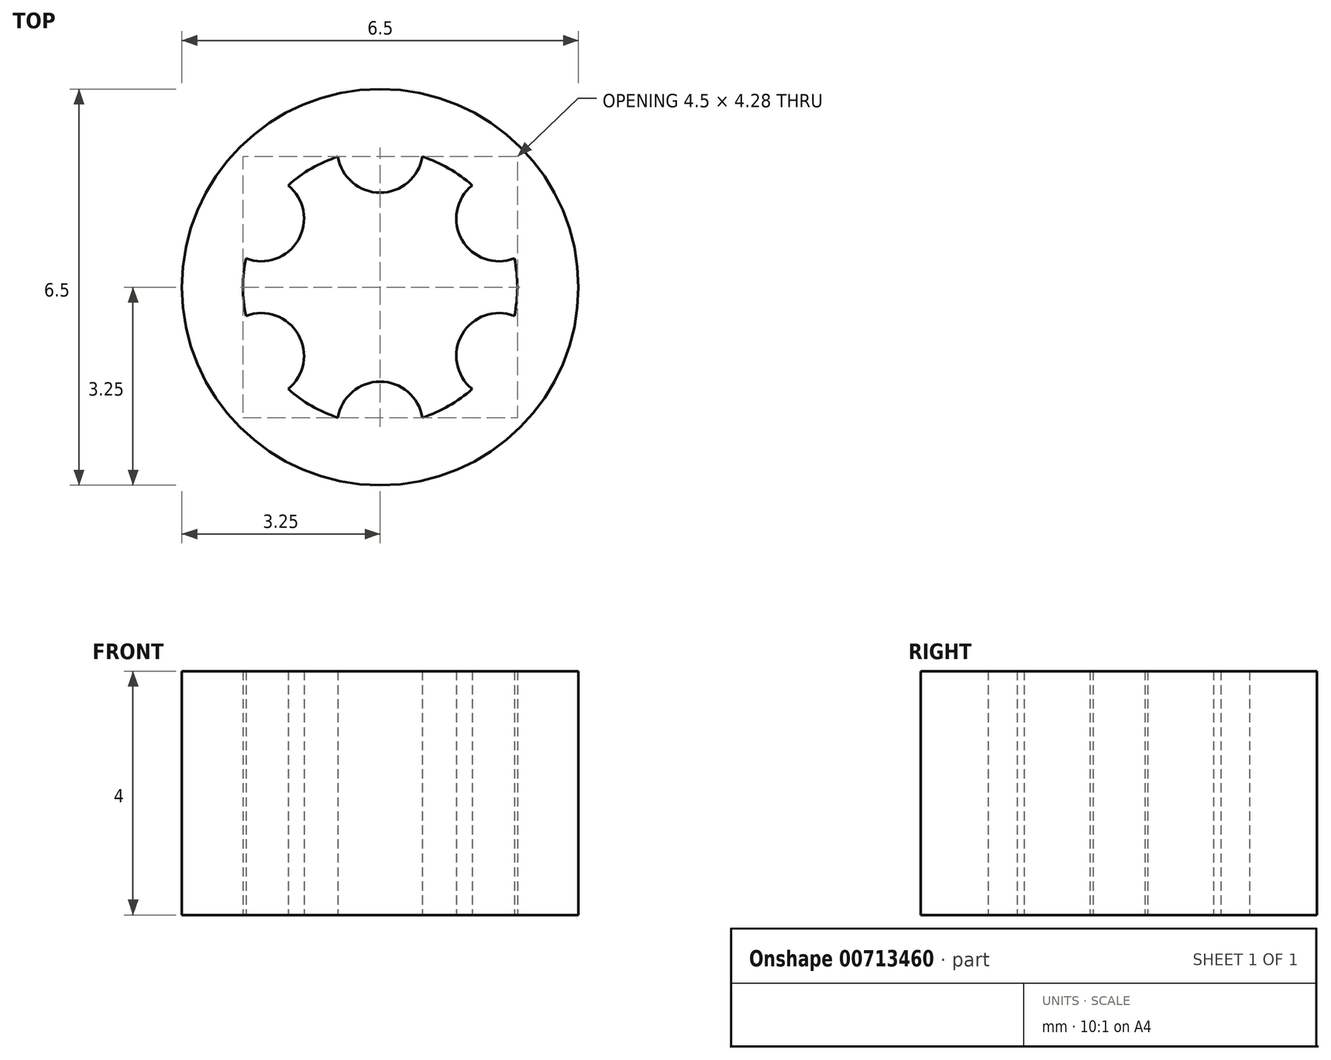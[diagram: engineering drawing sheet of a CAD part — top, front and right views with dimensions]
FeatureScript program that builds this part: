
annotation { "Feature Type Name" : "Feature", "Feature Type Description" : "" }
export const myFeature = defineFeature(function(context is Context, id is Id, definition is map)
    precondition{}
    {
        {
            var Q0;
            Q0=qCreatedBy(makeId("Top.planeOp"),FACE);
            var sketch = newSketch(context, id + "F0", { "sketchPlane" : qUnion([Q0])});
            skCircle(sketch, "E0", {"center": v(0, 0) * mm, "radius": 2.25 * mm});
            skCircle(sketch, "E1", {"center": v(0, 0) * mm, "radius": 3.25 * mm});
            skCircle(sketch, "E2", {"center": v(0, 2.25) * mm, "radius": 0.7 * mm});
            skCircle(sketch, "E3.1.0", {"center": v(-1.95, 1.13) * mm, "radius": 0.7 * mm});
            skCircle(sketch, "E3.2.0", {"center": v(-1.95, -1.12) * mm, "radius": 0.7 * mm});
            skCircle(sketch, "E3.3.0", {"center": v(0, -2.25) * mm, "radius": 0.7 * mm});
            skCircle(sketch, "E3.4.0", {"center": v(1.95, -1.13) * mm, "radius": 0.7 * mm});
            skCircle(sketch, "E3.5.0", {"center": v(1.95, 1.13) * mm, "radius": 0.7 * mm});
            skSolve(sketch);
        }
        {
            var Q0;
            Q0=qSketchRegion(id+"F0",true);
            var Q1;
            {var subQ0=sQuery(id+"F0.wireOp",EDGE,"E3.1.0");var subQ1=sQuery(id+"F0.wireOp",EDGE,"E0");var subQ2=makeQuery(id+"F0.imprint","INTERSECT",VERTEX,{"disambiguationData":[OD(0.0)],"derivedFrom":[subQ1,subQ0]});Q1=makeQuery(id+"F0.imprint","IMPRINT",FACE,{"disambiguationData":[TD([[makeQuery(id+"F0.imprint","IMPRINT",EDGE,{"disambiguationData":[TD([[subQ2,-1.0]])],"derivedFrom":subQ1}),1.0]])]});}
            var Q2;
            {var subQ0=sQuery(id+"F0.wireOp",EDGE,"E3.1.0");var subQ1=sQuery(id+"F0.wireOp",EDGE,"E0");var subQ2=makeQuery(id+"F0.imprint","INTERSECT",VERTEX,{"disambiguationData":[OD(0.0)],"derivedFrom":[subQ1,subQ0]});Q2=makeQuery(id+"F0.imprint","IMPRINT",FACE,{"disambiguationData":[TD([[makeQuery(id+"F0.imprint","IMPRINT",EDGE,{"disambiguationData":[TD([[subQ2,-1.0]])],"derivedFrom":subQ1}),-1.0]])]});}
            var Q3;
            {var subQ0=sQuery(id+"F0.wireOp",EDGE,"E2");var subQ1=sQuery(id+"F0.wireOp",EDGE,"E0");var subQ2=makeQuery(id+"F0.imprint","INTERSECT",VERTEX,{"disambiguationData":[OD(0.0)],"derivedFrom":[subQ1,subQ0]});Q3=makeQuery(id+"F0.imprint","IMPRINT",FACE,{"disambiguationData":[TD([[makeQuery(id+"F0.imprint","IMPRINT",EDGE,{"disambiguationData":[TD([[subQ2,-1.0]])],"derivedFrom":subQ1}),-1.0]])]});}
            var Q4;
            {var subQ0=sQuery(id+"F0.wireOp",EDGE,"E2");var subQ1=sQuery(id+"F0.wireOp",EDGE,"E0");var subQ2=makeQuery(id+"F0.imprint","INTERSECT",VERTEX,{"disambiguationData":[OD(0.0)],"derivedFrom":[subQ1,subQ0]});Q4=makeQuery(id+"F0.imprint","IMPRINT",FACE,{"disambiguationData":[TD([[makeQuery(id+"F0.imprint","IMPRINT",EDGE,{"disambiguationData":[TD([[subQ2,-1.0]])],"derivedFrom":subQ1}),1.0]])]});}
            var Q5;
            {var subQ0=sQuery(id+"F0.wireOp",EDGE,"E3.5.0");var subQ1=sQuery(id+"F0.wireOp",EDGE,"E0");var subQ2=makeQuery(id+"F0.imprint","INTERSECT",VERTEX,{"disambiguationData":[OD(0.0)],"derivedFrom":[subQ1,subQ0]});Q5=makeQuery(id+"F0.imprint","IMPRINT",FACE,{"disambiguationData":[TD([[makeQuery(id+"F0.imprint","IMPRINT",EDGE,{"disambiguationData":[TD([[subQ2,1.0]])],"derivedFrom":subQ1}),-1.0]])]});}
            var Q6;
            {var subQ0=sQuery(id+"F0.wireOp",EDGE,"E3.5.0");var subQ1=sQuery(id+"F0.wireOp",EDGE,"E0");var subQ2=makeQuery(id+"F0.imprint","INTERSECT",VERTEX,{"disambiguationData":[OD(0.0)],"derivedFrom":[subQ1,subQ0]});Q6=makeQuery(id+"F0.imprint","IMPRINT",FACE,{"disambiguationData":[TD([[makeQuery(id+"F0.imprint","IMPRINT",EDGE,{"disambiguationData":[TD([[subQ2,1.0]])],"derivedFrom":subQ1}),1.0]])]});}
            var Q7;
            {var subQ0=sQuery(id+"F0.wireOp",EDGE,"E3.4.0");var subQ1=sQuery(id+"F0.wireOp",EDGE,"E0");var subQ2=makeQuery(id+"F0.imprint","INTERSECT",VERTEX,{"disambiguationData":[OD(0.0)],"derivedFrom":[subQ1,subQ0]});Q7=makeQuery(id+"F0.imprint","IMPRINT",FACE,{"disambiguationData":[TD([[makeQuery(id+"F0.imprint","IMPRINT",EDGE,{"disambiguationData":[TD([[subQ2,-1.0]])],"derivedFrom":subQ1}),-1.0]])]});}
            var Q8;
            {var subQ0=sQuery(id+"F0.wireOp",EDGE,"E3.3.0");var subQ1=sQuery(id+"F0.wireOp",EDGE,"E0");var subQ2=makeQuery(id+"F0.imprint","INTERSECT",VERTEX,{"disambiguationData":[OD(0.0)],"derivedFrom":[subQ1,subQ0]});Q8=makeQuery(id+"F0.imprint","IMPRINT",FACE,{"disambiguationData":[TD([[makeQuery(id+"F0.imprint","IMPRINT",EDGE,{"disambiguationData":[TD([[subQ2,-1.0]])],"derivedFrom":subQ1}),-1.0]])]});}
            var Q9;
            {var subQ0=sQuery(id+"F0.wireOp",EDGE,"E3.2.0");var subQ1=sQuery(id+"F0.wireOp",EDGE,"E0");var subQ2=makeQuery(id+"F0.imprint","INTERSECT",VERTEX,{"disambiguationData":[OD(0.0)],"derivedFrom":[subQ1,subQ0]});Q9=makeQuery(id+"F0.imprint","IMPRINT",FACE,{"disambiguationData":[TD([[makeQuery(id+"F0.imprint","IMPRINT",EDGE,{"disambiguationData":[TD([[subQ2,-1.0]])],"derivedFrom":subQ1}),-1.0]])]});}
            var Q10;
            {var subQ0=sQuery(id+"F0.wireOp",EDGE,"E3.3.0");var subQ1=sQuery(id+"F0.wireOp",EDGE,"E0");var subQ2=makeQuery(id+"F0.imprint","INTERSECT",VERTEX,{"disambiguationData":[OD(0.0)],"derivedFrom":[subQ1,subQ0]});Q10=makeQuery(id+"F0.imprint","IMPRINT",FACE,{"disambiguationData":[TD([[makeQuery(id+"F0.imprint","IMPRINT",EDGE,{"disambiguationData":[TD([[subQ2,-1.0]])],"derivedFrom":subQ1}),1.0]])]});}
            var Q11;
            {var subQ0=sQuery(id+"F0.wireOp",EDGE,"E3.2.0");var subQ1=sQuery(id+"F0.wireOp",EDGE,"E0");var subQ2=makeQuery(id+"F0.imprint","INTERSECT",VERTEX,{"disambiguationData":[OD(0.0)],"derivedFrom":[subQ1,subQ0]});Q11=makeQuery(id+"F0.imprint","IMPRINT",FACE,{"disambiguationData":[TD([[makeQuery(id+"F0.imprint","IMPRINT",EDGE,{"disambiguationData":[TD([[subQ2,-1.0]])],"derivedFrom":subQ1}),1.0]])]});}
            var Q12;
            {var subQ0=sQuery(id+"F0.wireOp",EDGE,"E3.4.0");var subQ1=sQuery(id+"F0.wireOp",EDGE,"E0");var subQ2=makeQuery(id+"F0.imprint","INTERSECT",VERTEX,{"disambiguationData":[OD(0.0)],"derivedFrom":[subQ1,subQ0]});Q12=makeQuery(id+"F0.imprint","IMPRINT",FACE,{"disambiguationData":[TD([[makeQuery(id+"F0.imprint","IMPRINT",EDGE,{"disambiguationData":[TD([[subQ2,-1.0]])],"derivedFrom":subQ1}),1.0]])]});}
            extrude(context, id + "F1", {"entities" : qUnion([Q0, Q1, Q2, Q3, Q4, Q5, Q6, Q7, Q8, Q9, Q10, Q11, Q12]), "depth" : 4 * mm, "offsetDistance" : 25 * mm});
        }
    });
